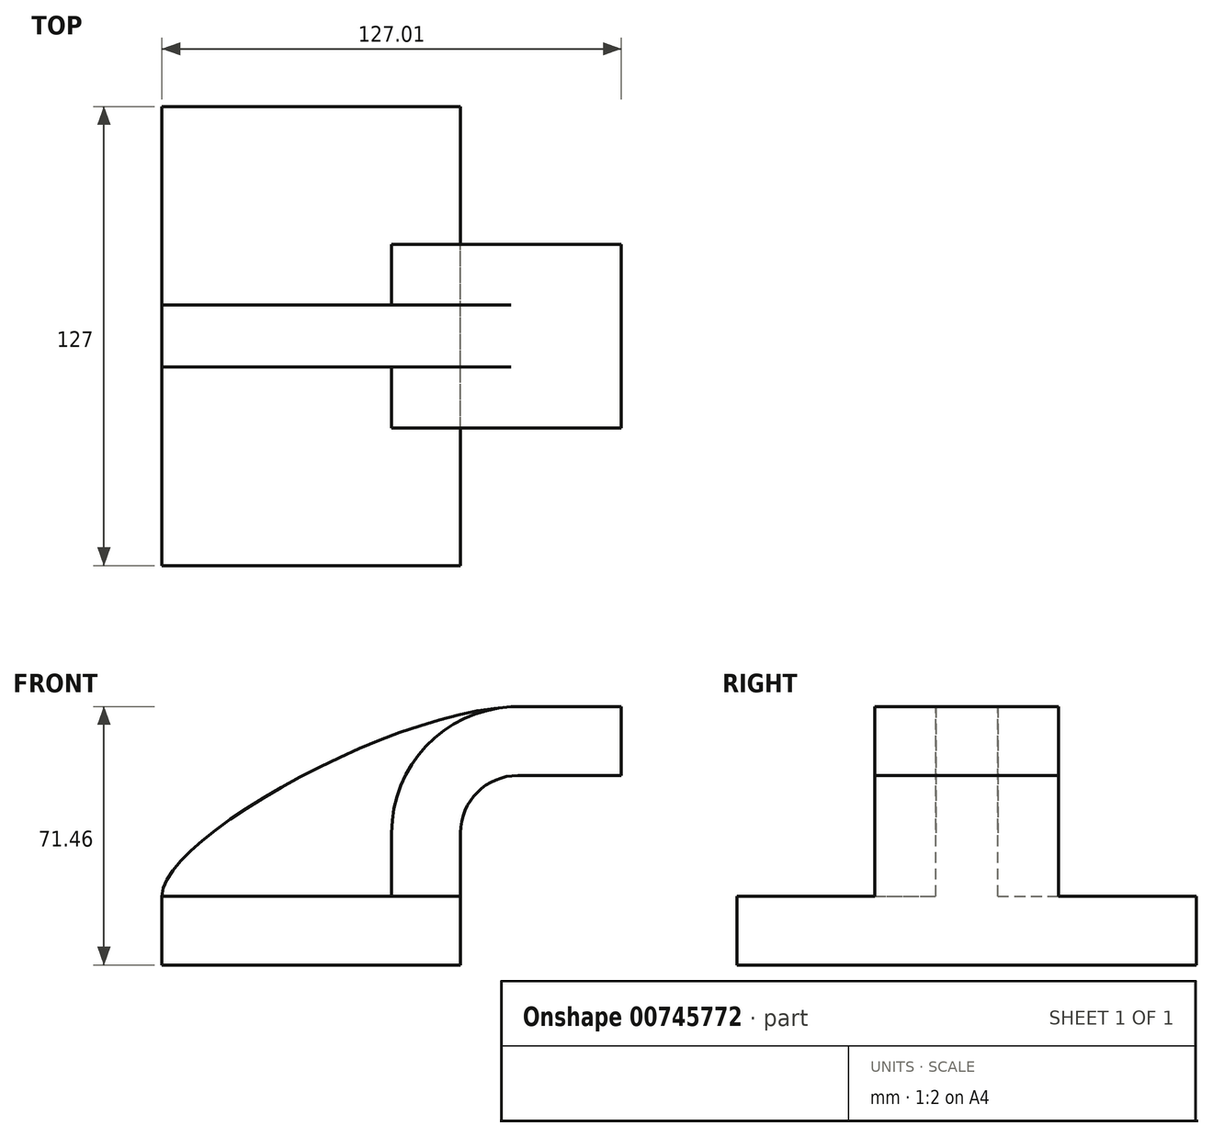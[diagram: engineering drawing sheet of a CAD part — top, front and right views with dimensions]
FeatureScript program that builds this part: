
annotation { "Feature Type Name" : "Feature", "Feature Type Description" : "" }
export const myFeature = defineFeature(function(context is Context, id is Id, definition is map)
    precondition{}
    {
        {
            var Q0;
            Q0=qCreatedBy(makeId("Front.planeOp"),FACE);
            var sketch = newSketch(context, id + "F0", { "sketchPlane" : qUnion([Q0])});
            skLineSegment(sketch, "E0.bottom", {"start": v(-41.28, 9.52) * mm, "end": v(41.28, 9.53) * mm});
            skLineSegment(sketch, "E0.top", {"start": v(-41.28, -9.53) * mm, "end": v(41.28, -9.53) * mm});
            skLineSegment(sketch, "E0.left", {"start": v(-41.28, 9.52) * mm, "end": v(-41.28, -9.53) * mm});
            skLineSegment(sketch, "E0.right", {"start": v(41.28, 9.53) * mm, "end": v(41.28, -9.52) * mm});
            skPoint(sketch, "E0.middle", {"position": v(0, 0) * mm});
            skLineSegment(sketch, "E1.bottom", {"start": v(111.23, 38.1) * mm, "end": v(60.43, 38.1) * mm});
            skLineSegment(sketch, "E1.top", {"start": v(111.23, 66.67) * mm, "end": v(60.43, 66.67) * mm});
            skLineSegment(sketch, "E1.left", {"start": v(111.23, 38.1) * mm, "end": v(111.23, 66.67) * mm});
            skLineSegment(sketch, "E1.right", {"start": v(60.43, 38.1) * mm, "end": v(60.43, 66.67) * mm});
            skPoint(sketch, "E1.middle", {"position": v(85.83, 52.39) * mm});
            skLineSegment(sketch, "E2", {"start": v(41.27, 9.53) * mm, "end": v(41.27, 27) * mm});
            skArc(sketch, "E3", {"start": v(41.27, 27) * mm, "mid": v(45.92, 38.23) * mm, "end": v(57.15, 42.88) * mm});
            skLineSegment(sketch, "E4", {"start": v(57.15, 42.88) * mm, "end": v(85.72, 42.88) * mm});
            skLineSegment(sketch, "E5.0", {"start": v(57.15, 61.93) * mm, "end": v(85.72, 61.93) * mm});
            skArc(sketch, "E5.1", {"start": v(22.22, 27) * mm, "mid": v(32.45, 51.7) * mm, "end": v(57.15, 61.93) * mm});
            skLineSegment(sketch, "E5.2", {"start": v(22.22, 9.53) * mm, "end": v(22.22, 27) * mm});
            skLineSegment(sketch, "E6", {"start": v(85.72, 66.67) * mm, "end": v(85.72, 38.1) * mm});
            skPoint(sketch, "E6.startSnap0", {"position": v(85.83, 66.67) * mm});
            skFitSpline(sketch, "E7", {"points": [v(-41.28, 9.52) * mm, v(57.15, 61.93) * mm], "startDerivative": vector(0, 48.46) * mm, "endDerivative": vector(99.4, 0.8) * mm});
            skSolve(sketch);
        }
        {
            var Q0;
            Q0=makeQuery(id+"F0.imprint","IMPRINT",FACE,{"disambiguationData":[TD([[makeQuery(id+"F0.imprint","IMPRINT",EDGE,{"derivedFrom":sQuery(id+"F0.wireOp",EDGE,"E0.top")}),1.0]])]});
            extrude(context, id + "F1", {"entities" : qUnion([Q0]), "endBound" : BoundingType.SYMMETRIC, "depth" : 127 * mm, "offsetDistance" : 25.4 * mm});
        }
        {
            var Q0;
            {var subQ1=sQuery(id+"F0.wireOp",EDGE,"E2");Q0=makeQuery(id+"F0.imprint","IMPRINT",FACE,{"disambiguationData":[TD([[makeQuery(id+"F0.imprint","IMPRINT",EDGE,{"derivedFrom":subQ1}),1.0]])]});}
            var Q1;
            {var subQ0=sQuery(id+"F0.wireOp",EDGE,"E4");var subQ1=sQuery(id+"F0.wireOp",EDGE,"E1.right");var subQ2=makeQuery(id+"F0.imprint","INTERSECT",VERTEX,{"derivedFrom":[subQ1,subQ0]});Q1=makeQuery(id+"F0.imprint","IMPRINT",FACE,{"disambiguationData":[TD([[makeQuery(id+"F0.imprint","IMPRINT",EDGE,{"disambiguationData":[TD([[subQ2,-1.0]])],"derivedFrom":subQ1}),-1.0]])]});}
            extrude(context, id + "F2", {"entities" : qUnion([Q0, Q1]), "operationType" : NewBodyOperationType.ADD, "endBound" : BoundingType.SYMMETRIC, "depth" : 50.8 * mm, "offsetDistance" : 25.4 * mm});
        }
        {
            var Q0;
            {var subQ3=sQuery(id+"F0.wireOp",EDGE,"E5.2");Q0=makeQuery(id+"F0.imprint","IMPRINT",FACE,{"disambiguationData":[TD([[makeQuery(id+"F0.imprint","IMPRINT",EDGE,{"derivedFrom":subQ3}),1.0]])]});}
            extrude(context, id + "F3", {"entities" : qUnion([Q0]), "operationType" : NewBodyOperationType.ADD, "endBound" : BoundingType.SYMMETRIC, "depth" : 17.14 * mm, "offsetDistance" : 25.4 * mm});
        }
    });
